# Revit family: Legrand_Lighting_Management_DALI_Power_Supply_Ceiling
name_source: partatom
category: Dispositifs d'éclairage
units: mm (PartAtom-declared; Revit-internal decimal feet)

## family parameters
Conserver l'orientation des annotations = Non
Cote de connecteur circulaire = Utiliser le diamètre
Couper avec des vides une fois chargée = Non
Hôte = Face
Partagée = Non
Point de calcul de pièce = Non
Type d'élément = Normal

## types (2) — shared parameters
Collecteur de terre = Non
Colour = <Par catégorie>
Constant light control = Non
Cosses d'artère secondaire = Non
Dim function with dimmer basic element = Non
Elévation par défaut = 1219 mm
Fabricant = Legrand
Forced switch off = Non
General Conditions of Use = https://export.legrand.com
Gestion alarme = Non
HVAC-control = Non
Liaison neutre = Non
Remote operation = Non
Response value luminosity adjustable = Non
Response value sensitivity adjustable = Non
Suitable for wireless transmission = Non
URL = http://www.legrandoc.com
zero-valued in all types: Detection angle horizontal (MAX) (°), Detection angle horizontal (MIN) (°), Diameter detection range on floor (m), Max. duty cycle (mn), Max. starting current (A), Max. switching power (W), Max. transmission range frontally (m), Max. transmission range sideways (m), Maximum mounting height (m), Min. switch-on time (s), Nominal voltage (V), RAL-number (akin), Response value luminosity (MAX) (lx), Response value luminosity (MIN) (lx), Temperature (MAX) (°C), Temperature (MIN) (°C)

## per-type parameters (varying)
| type | Alimentation DALI | Boite de contrôle 2 sorties DALI | Degree of protection (IP) | Description | Frequency (MAX) (Hz) | Frequency (MIN) (Hz) | Model | Modèle | Mounting method | Substation input |
| DALI Power Supply | Oui | Non |  | DALI power supply - 230 V - 250 mA - 16 V= - for false ceiling | 0 | 0 |  | 003515 | Other | Non |
| Control Box 2 outputs DALI | Non | Oui | IP20 | DALI power supply - for Cat.Nos 0 489 35/36 - 16 DALI ballasts max. | 60 | 50 | Control module | 048876 | Surface mounted (plaster) | Oui |
